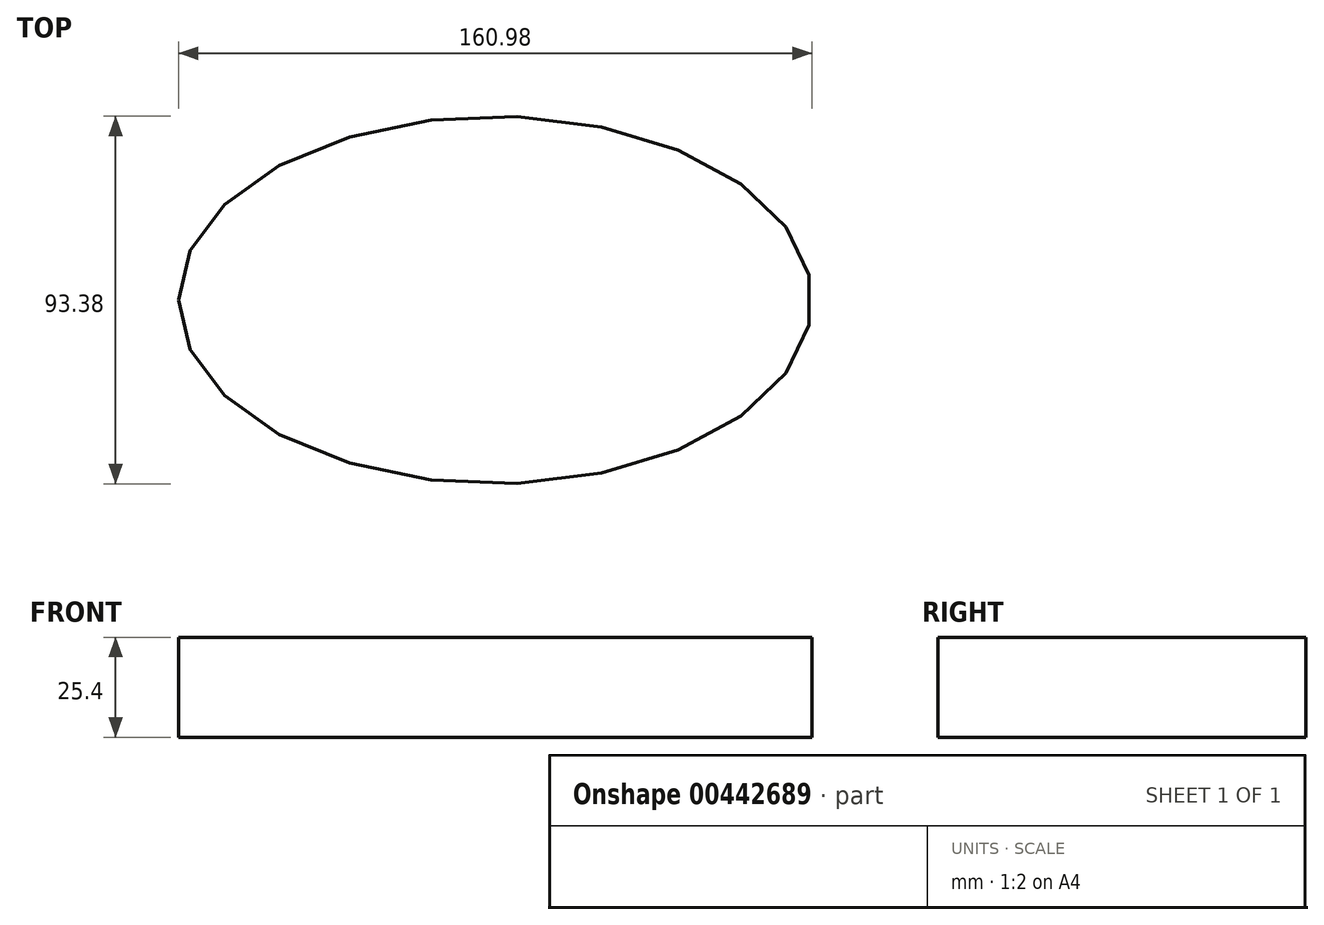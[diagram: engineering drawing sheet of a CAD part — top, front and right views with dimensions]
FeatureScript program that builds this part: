
annotation { "Feature Type Name" : "Feature", "Feature Type Description" : "" }
export const myFeature = defineFeature(function(context is Context, id is Id, definition is map)
    precondition{}
    {
        {
            var Q0;
            Q0=qCreatedBy(makeId("Top.planeOp"),FACE);
            var sketch = newSketch(context, id + "F0", { "sketchPlane" : qUnion([Q0])});
            skEllipse(sketch, "E0", {"center": v(0, 0) * mm, "majorRadius": 80.49 * mm, "minorRadius": 46.7 * mm, "majorAxis": v(-1, 0)});
            skSolve(sketch);
        }
        {
            var Q0;
            Q0 = qSketchRegion(id + "F0", true);
            extrude(context, id + "F1", {"entities" : qUnion([Q0]), "depth" : 25.4 * mm, "offsetDistance" : 25.4 * mm});
        }
    });
